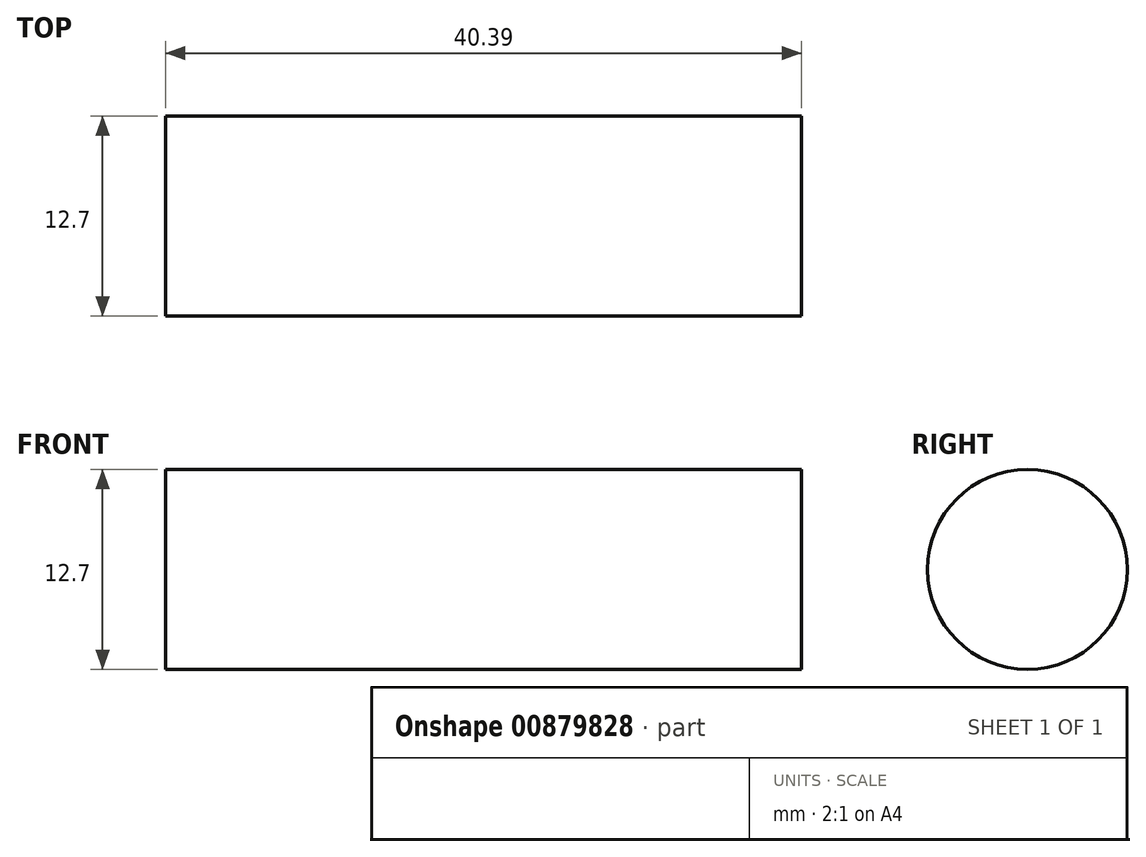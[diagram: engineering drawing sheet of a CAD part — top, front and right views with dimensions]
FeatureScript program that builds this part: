
annotation { "Feature Type Name" : "Feature", "Feature Type Description" : "" }
export const myFeature = defineFeature(function(context is Context, id is Id, definition is map)
    precondition{}
    {
        {
            var Q0;
            Q0=qCreatedBy(makeId("Right.planeOp"),FACE);
            var sketch = newSketch(context, id + "F0", { "sketchPlane" : qUnion([Q0])});
            skCircle(sketch, "E0", {"center": v(0, 0) * mm, "radius": 6.35 * mm});
            skSolve(sketch);
        }
        {
            var Q0;
            Q0 = qSketchRegion(id + "F0", true);
            extrude(context, id + "F1", {"entities" : qUnion([Q0]), "depth" : 40.4 * mm, "offsetDistance" : 25.4 * mm});
        }
    });
